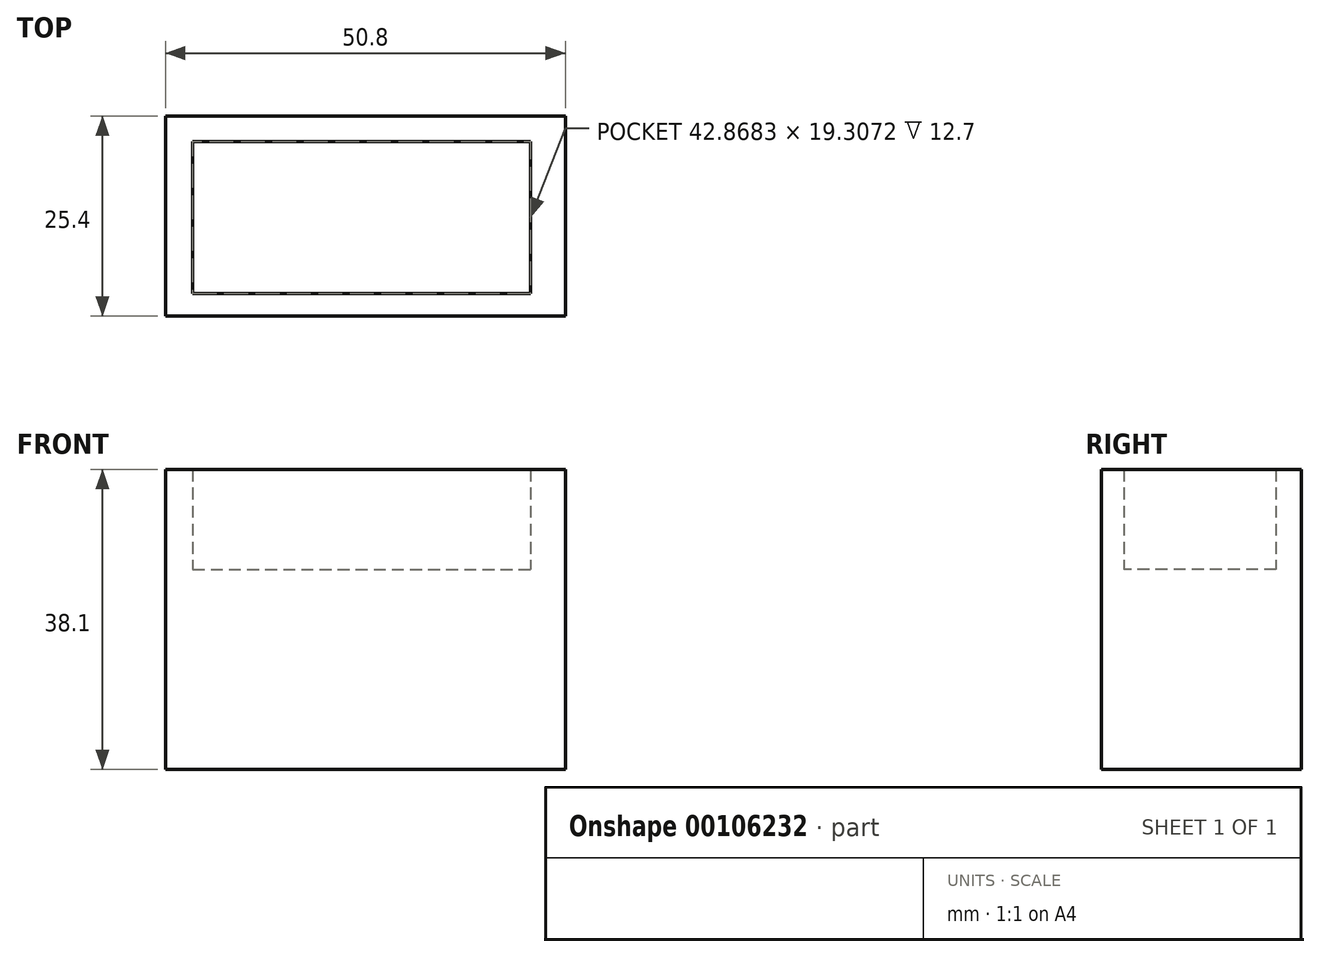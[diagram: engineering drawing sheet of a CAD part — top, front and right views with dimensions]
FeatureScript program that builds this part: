
annotation { "Feature Type Name" : "Feature", "Feature Type Description" : "" }
export const myFeature = defineFeature(function(context is Context, id is Id, definition is map)
    precondition{}
    {
        {
            var Q0;
            Q0=qCreatedBy(makeId("Top.planeOp"),FACE);
            var sketch = newSketch(context, id + "F0", { "sketchPlane" : qUnion([Q0])});
            skLineSegment(sketch, "E0.bottom", {"start": v(-19.35, 12.89) * mm, "end": v(31.45, 12.89) * mm});
            skLineSegment(sketch, "E0.top", {"start": v(-19.35, -12.51) * mm, "end": v(31.45, -12.51) * mm});
            skLineSegment(sketch, "E0.left", {"start": v(-19.35, 12.89) * mm, "end": v(-19.35, -12.51) * mm});
            skLineSegment(sketch, "E0.right", {"start": v(31.45, 12.89) * mm, "end": v(31.45, -12.51) * mm});
            skSolve(sketch);
        }
        {
            var Q0;
            Q0=makeQuery(id+"F0.imprint","IMPRINT",FACE,{"disambiguationData":[TD([[makeQuery(id+"F0.imprint","IMPRINT",EDGE,{"derivedFrom":sQuery(id+"F0.wireOp",EDGE,"E0.bottom")}),-1.0]])]});
            extrude(context, id + "F1", {"entities" : qUnion([Q0]), "depth" : 25.4 * mm});
        }
        {
            var Q0;
            Q0=makeQuery(id+"F1.opExtrude","CAP_FACE",FACE,{"disambiguationData":[OSD([sQuery(id+"F0.wireOp",EDGE,"E0.bottom"),sQuery(id+"F0.wireOp",EDGE,"E0.top"),sQuery(id+"F0.wireOp",EDGE,"E0.left"),sQuery(id+"F0.wireOp",EDGE,"E0.right")])],"isStart":false});
            var sketch = newSketch(context, id + "F2", { "sketchPlane" : qUnion([Q0])});
            skLineSegment(sketch, "E1.bottom", {"start": v(-19.35, 12.89) * mm, "end": v(-15.87, 12.89) * mm});
            skLineSegment(sketch, "E1.top", {"start": v(-19.35, -12.51) * mm, "end": v(-15.87, -12.51) * mm});
            skLineSegment(sketch, "E1.left", {"start": v(-19.35, 12.89) * mm, "end": v(-19.35, -12.51) * mm});
            skLineSegment(sketch, "E2.bottom", {"start": v(-19.35, 12.89) * mm, "end": v(31.45, 12.89) * mm});
            skLineSegment(sketch, "E2.top", {"start": v(-19.35, 9.65) * mm, "end": v(31.45, 9.65) * mm});
            skLineSegment(sketch, "E2.left", {"start": v(-19.35, 12.89) * mm, "end": v(-19.35, 9.65) * mm});
            skLineSegment(sketch, "E2.right", {"start": v(31.45, 12.89) * mm, "end": v(31.45, 9.65) * mm});
            skLineSegment(sketch, "E3.bottom", {"start": v(-19.35, -12.51) * mm, "end": v(31.45, -12.51) * mm});
            skLineSegment(sketch, "E3.top", {"start": v(-19.35, -9.65) * mm, "end": v(31.45, -9.65) * mm});
            skLineSegment(sketch, "E3.left", {"start": v(-19.35, -12.51) * mm, "end": v(-19.35, -9.65) * mm});
            skLineSegment(sketch, "E3.right", {"start": v(31.45, -12.51) * mm, "end": v(31.45, -9.65) * mm});
            skLineSegment(sketch, "E4.bottom", {"start": v(27, 12.89) * mm, "end": v(31.45, 12.89) * mm});
            skLineSegment(sketch, "E4.top", {"start": v(27, -12.51) * mm, "end": v(31.45, -12.51) * mm});
            skLineSegment(sketch, "E4.left", {"start": v(27, 12.89) * mm, "end": v(27, -12.51) * mm});
            skLineSegment(sketch, "E4.right", {"start": v(31.45, 12.89) * mm, "end": v(31.45, -12.51) * mm});
            skLineSegment(sketch, "E5", {"start": v(-15.87, 12.89) * mm, "end": v(-15.87, -12.51) * mm});
            skSolve(sketch);
        }
        {
            var Q0;
            Q0 = qSketchRegion(id + "F2", true);
            extrude(context, id + "F3", {"entities" : qUnion([Q0]), "operationType" : NewBodyOperationType.ADD, "depth" : 12.7 * mm});
        }
    });
